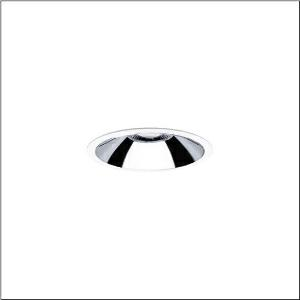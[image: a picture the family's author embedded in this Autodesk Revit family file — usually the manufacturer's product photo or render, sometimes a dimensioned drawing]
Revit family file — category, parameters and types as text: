
# Revit family: lunis_21_l_51db15dd42
name_source: partatom
category: Lighting Fixtures
units: mm (PartAtom-declared; Revit-internal decimal feet)

## family parameters
Cut with Voids When Loaded = No
Host = Face
Light Source = No
Part Type = Normal
Room Calculation Point = No
Round Connector Dimension = Use Diameter
Shared = No

## types (1)
- Lunis 21 L (1 x LED, 1700 lm, 13.8 W, 4000K)
    Apparent Load = 14 VA
    CIE Flux Codes = 90 99 100 100 100
    Color Rendering = 80
    Color Temperature = 4000K
    Default Elevation = 1800 mm
    Description = Lunis 21,  L, downlight, of PC, light emission: direct distribution, LED rated luminous flux: 1.700lm, light colour: 840, control gear: ECG DALI, with terminal, 5-pole, mains connection: 220..240V, AC, housing, round, of diecast aluminium, traffic white (RAL 9016), diameter: 162mm, protection rating (complete): IP20, protection rating (on room side): IP54, insulation class (complete): insulation class II (safety insulation), certification: CE, impact resistance: IK02, packaging unit: 1 piece
    Height = 0 mm  [stored 0 ft]
    Lamp = 1 x LED
    Lamp Light Flux = 1700 lm
    Lamp Power = 13.8 W
    Lamp count = 1
    Length = 162 mm
    Luminous efficacy = 123 lm/W
    Manufacturer = Siteco
    ModVariant = No
    Model = 51DB15DD42
    Mounting Place = Ceiling
    Mounting Type = Recessed
    Number of Poles = 1
    OnlyDefault = Yes
    Power Factor = 1
    Product Name = Lunis 21 L
    Product group = downlight
    ProductGroupID = 400
    Protection Class = Protection class II
    Protection Degree = IP 20
    RLX_Detail_Level = 1
    RLX_Emergency_Light_Flux = 0 lm
    RLX_Emergency_Type = 0
    RLX_Emergency_Type_DB = No
    RlxData = <blob elided: 21253 chars, md5=94836489>
    Socket = socket
    Standby Power = 0 W
    System Light Flux = 1700 lm
    System Power = 14 W
    Type Comments = Product without accessories
    Type Image = l_1287387.jpg
    URL = http://relux.com
    VarID = ---
    Voltage = 0 V
    Weight = 0.00 kg
    Width = 0 mm  [stored 0 ft]

note: [stored X ft] marks values corroborated as IEEE doubles in the binary element streams (Revit-internal decimal feet)

## geometry (parser evidence)
native form markers: Blend x4, Sweep x9
no freeform markers — native parametric forms only
